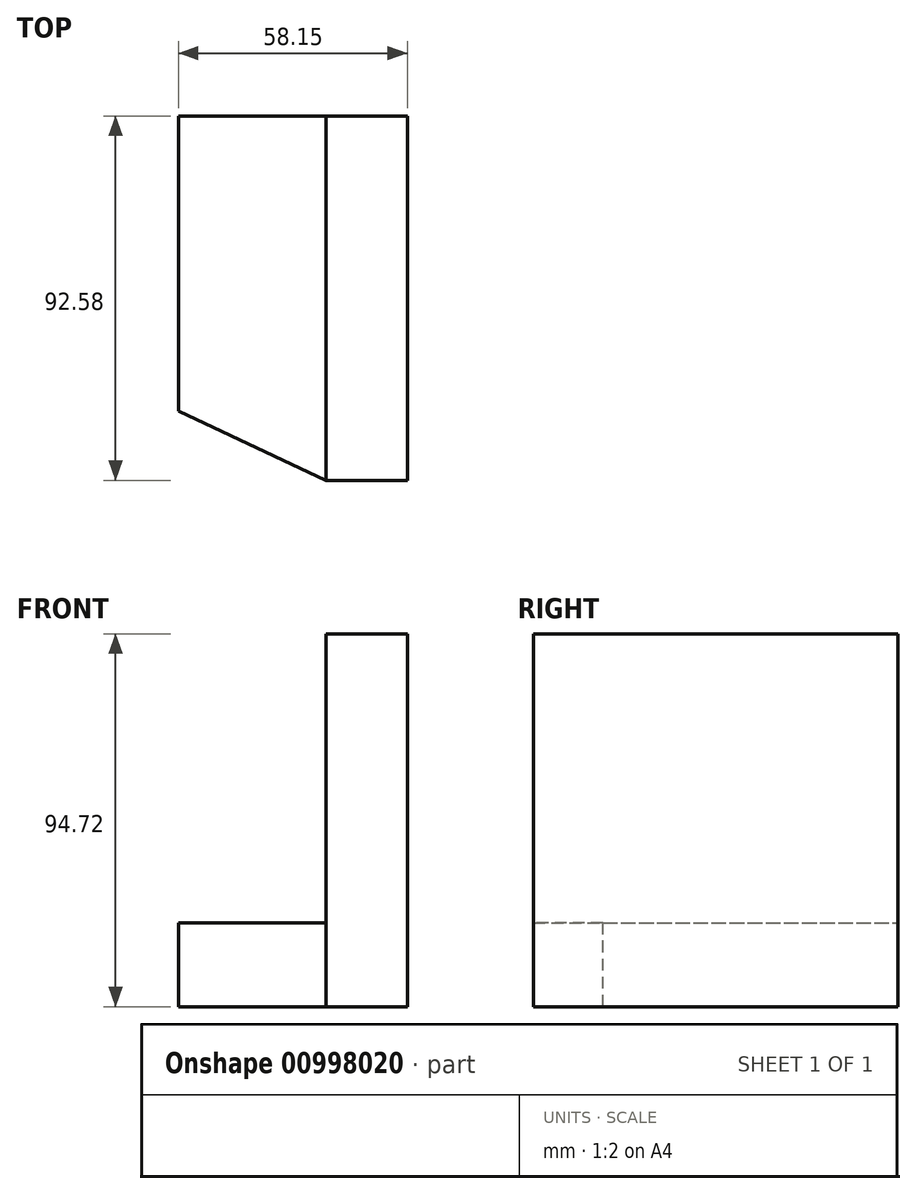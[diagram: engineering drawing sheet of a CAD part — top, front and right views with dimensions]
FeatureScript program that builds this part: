
annotation { "Feature Type Name" : "Feature", "Feature Type Description" : "" }
export const myFeature = defineFeature(function(context is Context, id is Id, definition is map)
    precondition{}
    {
        {
            var Q0;
            Q0=qCreatedBy(makeId("Front.planeOp"),FACE);
            var sketch = newSketch(context, id + "F0", { "sketchPlane" : qUnion([Q0])});
            skLineSegment(sketch, "E0.bottom", {"start": v(-34.14, 31.9) * mm, "end": v(-13.47, 31.9) * mm});
            skLineSegment(sketch, "E0.top", {"start": v(-34.14, -62.83) * mm, "end": v(-13.47, -62.83) * mm});
            skLineSegment(sketch, "E0.left", {"start": v(-34.14, 31.9) * mm, "end": v(-34.14, -62.83) * mm});
            skLineSegment(sketch, "E0.right", {"start": v(-13.47, 31.9) * mm, "end": v(-13.47, -62.83) * mm});
            skPoint(sketch, "E1.firstSnap0", {"position": v(-13.47, -15.47) * mm});
            skLineSegment(sketch, "E1.bottom", {"start": v(-13.47, 0) * mm, "end": v(0, 0) * mm});
            skLineSegment(sketch, "E1.top", {"start": v(-13.47, -26.62) * mm, "end": v(0, -26.62) * mm});
            skLineSegment(sketch, "E1.left", {"start": v(-13.47, 0) * mm, "end": v(-13.47, -26.62) * mm});
            skLineSegment(sketch, "E1.right", {"start": v(0, 0) * mm, "end": v(0, -26.62) * mm});
            skLineSegment(sketch, "E2", {"start": v(0, 73.43) * mm, "end": v(0, -71.42) * mm, "construction": true});
            skLineSegment(sketch, "E3.MirrorCS", {"start": v(13.47, 0) * mm, "end": v(0, 0) * mm});
            skLineSegment(sketch, "E4.MirrorCS", {"start": v(13.47, -26.62) * mm, "end": v(0, -26.62) * mm});
            skLineSegment(sketch, "E5.MirrorCS", {"start": v(34.14, 31.9) * mm, "end": v(34.14, -62.83) * mm});
            skLineSegment(sketch, "E6.MirrorCS", {"start": v(34.14, -62.83) * mm, "end": v(13.47, -62.83) * mm});
            skLineSegment(sketch, "E7.MirrorCS", {"start": v(13.47, 31.9) * mm, "end": v(13.47, -62.83) * mm});
            skLineSegment(sketch, "E8.MirrorCS", {"start": v(34.14, 31.9) * mm, "end": v(13.47, 31.9) * mm});
            skSolve(sketch);
        }
        {
            var Q0;
            Q0 = qSketchRegion(id + "F0", true);
            var sketch = newSketch(context, id + "F1", { "sketchPlane" : qUnion([Q0])});
            skSolve(sketch);
        }
        {
            var Q0;
            Q0=makeQuery(id+"F1.imprint","IMPRINT",FACE,{"disambiguationData":[TD([[makeQuery(id+"F1.imprint","IMPRINT",EDGE,{"derivedFrom":makeQuery(id+"F0.imprint","IMPRINT",EDGE,{"derivedFrom":sQuery(id+"F0.wireOp",EDGE,"E5.MirrorCS")})}),-1.0]])]});
            var Q1;
            Q1=makeQuery(id+"F1.imprint","IMPRINT",FACE,{"disambiguationData":[TD([[makeQuery(id+"F1.imprint","IMPRINT",EDGE,{"derivedFrom":makeQuery(id+"F0.imprint","IMPRINT",EDGE,{"derivedFrom":sQuery(id+"F0.wireOp",EDGE,"E1.right")})}),1.0]])]});
            var Q2;
            Q2=makeQuery(id+"F1.imprint","IMPRINT",FACE,{"disambiguationData":[TD([[makeQuery(id+"F1.imprint","IMPRINT",EDGE,{"derivedFrom":makeQuery(id+"F0.imprint","IMPRINT",EDGE,{"derivedFrom":sQuery(id+"F0.wireOp",EDGE,"E1.bottom")})}),-1.0]])]});
            var Q3;
            {var subQ1=sQuery(id+"F0.wireOp",EDGE,"E0.bottom");Q3=makeQuery(id+"F1.imprint","IMPRINT",FACE,{"disambiguationData":[TD([[makeQuery(id+"F1.imprint","IMPRINT",EDGE,{"derivedFrom":makeQuery(id+"F0.imprint","IMPRINT",EDGE,{"derivedFrom":subQ1})}),-1.0]])]});}
            extrude(context, id + "F2", {"entities" : qUnion([Q0, Q1, Q2, Q3]), "oppositeDirection" : true, "depth" : 92.58 * mm, "offsetDistance" : 25.4 * mm});
        }
        {
            var Q0;
            Q0=makeQuery(id+"F2.opExtrude","SWEPT_FACE",FACE,{"disambiguationData":[OSD([sQuery(id+"F0.wireOp",EDGE,"E0.left")])]});
            var sketch = newSketch(context, id + "F3", { "sketchPlane" : qUnion([Q0])});
            skLineSegment(sketch, "E9", {"start": v(0, -62.83) * mm, "end": v(0, -41.6) * mm});
            skLineSegment(sketch, "E10", {"start": v(0, -41.6) * mm, "end": v(-92.58, -41.6) * mm});
            skLineSegment(sketch, "E11", {"start": v(-92.58, -41.6) * mm, "end": v(-92.58, -62.83) * mm});
            skSolve(sketch);
        }
        {
            var Q0;
            Q0=makeQuery(id+"F3.imprint","IMPRINT",FACE,{"disambiguationData":[TD([[makeQuery(id+"F3.imprint","IMPRINT",EDGE,{"derivedFrom":sQuery(id+"F3.wireOp",EDGE,"E9")}),-1.0]])]});
            extrude(context, id + "F4", {"entities" : qUnion([Q0]), "operationType" : NewBodyOperationType.ADD, "depth" : 37.48 * mm, "offsetDistance" : 25.4 * mm});
        }
        {
            var Q0;
            Q0=makeQuery(id+"F4.opExtrude","SWEPT_FACE",FACE,{"disambiguationData":[OSD([sQuery(id+"F3.wireOp",EDGE,"E10")])]});
            var sketch = newSketch(context, id + "F5", { "sketchPlane" : qUnion([Q0])});
            skLineSegment(sketch, "E12", {"start": v(-34.14, 0) * mm, "end": v(-71.62, 0) * mm});
            skLineSegment(sketch, "E13", {"start": v(-71.62, 0) * mm, "end": v(-71.62, 17.65) * mm});
            skLineSegment(sketch, "E14", {"start": v(-71.62, 17.65) * mm, "end": v(-34.14, 0) * mm});
            skSolve(sketch);
        }
        {
            var Q0;
            Q0=makeQuery(id+"F5.imprint","IMPRINT",FACE,{"disambiguationData":[TD([[makeQuery(id+"F5.imprint","IMPRINT",EDGE,{"derivedFrom":sQuery(id+"F5.wireOp",EDGE,"E12")}),1.0]])]});
            extrude(context, id + "F6", {"entities" : qUnion([Q0]), "operationType" : NewBodyOperationType.REMOVE, "oppositeDirection" : true, "depth" : 116.45 * mm, "offsetDistance" : 25.4 * mm});
        }
    });
